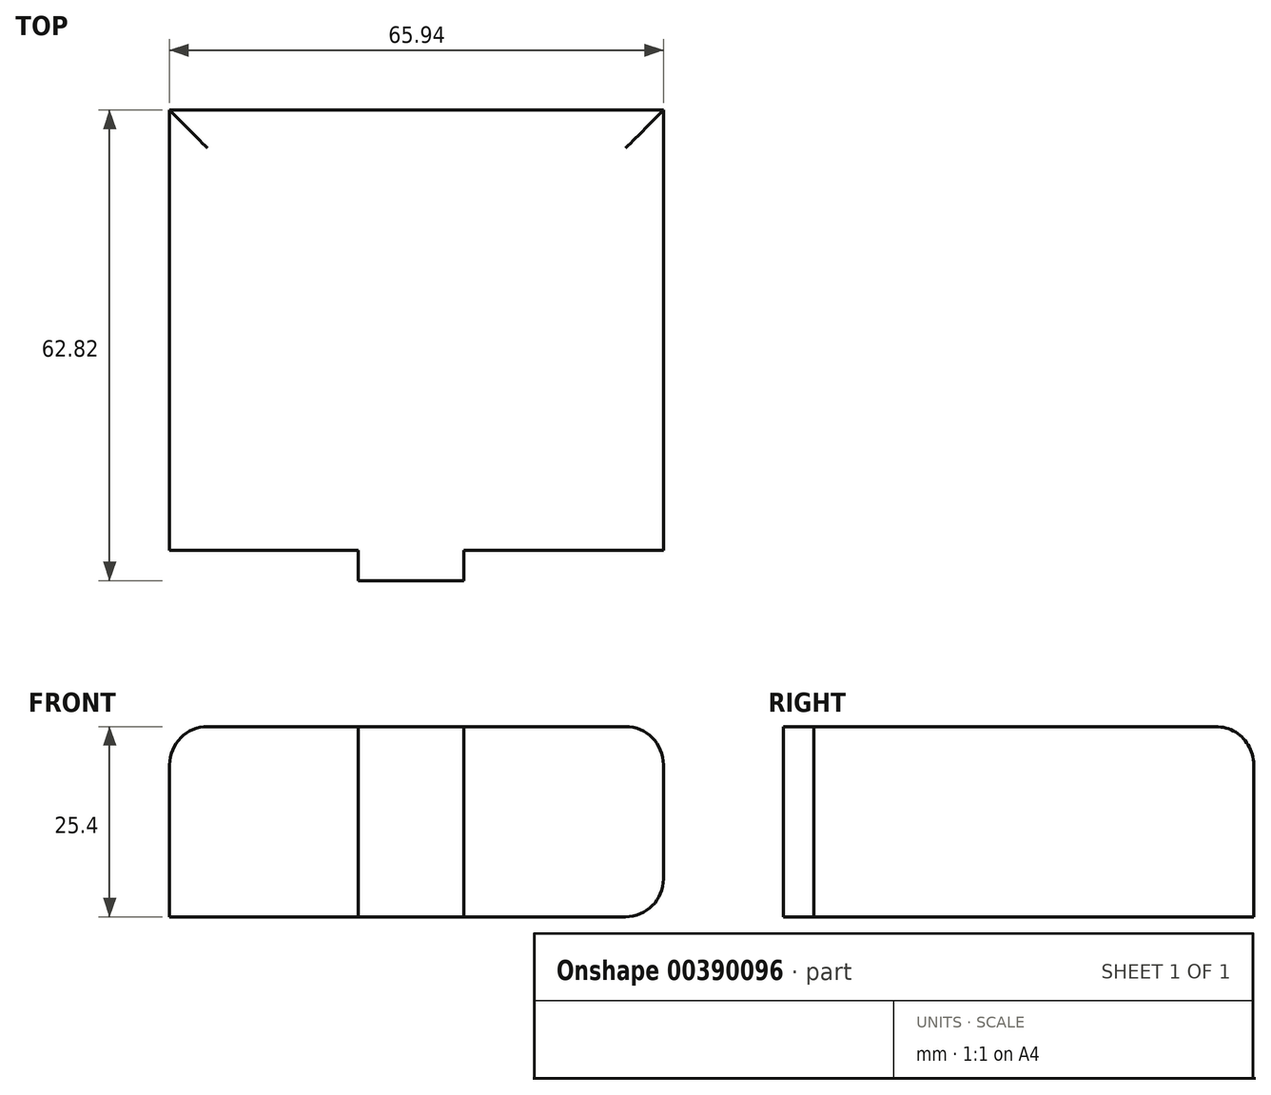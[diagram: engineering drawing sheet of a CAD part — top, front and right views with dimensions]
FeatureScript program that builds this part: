
annotation { "Feature Type Name" : "Feature", "Feature Type Description" : "" }
export const myFeature = defineFeature(function(context is Context, id is Id, definition is map)
    precondition{}
    {
        {
            var Q0;
            Q0=qCreatedBy(makeId("Top.planeOp"),FACE);
            var sketch = newSketch(context, id + "F0", { "sketchPlane" : qUnion([Q0])});
            skLineSegment(sketch, "E0.bottom", {"start": v(-14.1, 65.47) * mm, "end": v(0, 65.47) * mm});
            skLineSegment(sketch, "E0.top", {"start": v(-14.1, 48) * mm, "end": v(0, 48) * mm});
            skLineSegment(sketch, "E0.left", {"start": v(-14.1, 65.47) * mm, "end": v(-14.1, 48) * mm});
            skLineSegment(sketch, "E0.right", {"start": v(0, 65.47) * mm, "end": v(0, 48) * mm});
            skLineSegment(sketch, "E1.bottom", {"start": v(26.66, 52.08) * mm, "end": v(-39.28, 52.08) * mm});
            skLineSegment(sketch, "E1.top", {"start": v(26.66, 110.83) * mm, "end": v(-39.28, 110.83) * mm});
            skLineSegment(sketch, "E1.left", {"start": v(26.66, 52.08) * mm, "end": v(26.66, 110.83) * mm});
            skLineSegment(sketch, "E1.right", {"start": v(-39.28, 52.08) * mm, "end": v(-39.28, 110.83) * mm});
            skSolve(sketch);
        }
        {
            var Q0;
            Q0 = qSketchRegion(id + "F0", true);
            extrude(context, id + "F1", {"entities" : qUnion([Q0]), "depth" : 25.4 * mm});
        }
        {
            var Q0;
            Q0=makeQuery(id+"F1.opExtrude","CAP_EDGE",EDGE,{"disambiguationData":[OSD([sQuery(id+"F0.wireOp",EDGE,"E1.left")])],"isStart":false});
            var Q1;
            Q1=makeQuery(id+"F1.opExtrude","CAP_EDGE",EDGE,{"disambiguationData":[OSD([sQuery(id+"F0.wireOp",EDGE,"E1.left")])],"isStart":true});
            var Q2;
            Q2=makeQuery(id+"F1.opExtrude","CAP_EDGE",EDGE,{"disambiguationData":[OSD([sQuery(id+"F0.wireOp",EDGE,"E1.right")])],"isStart":false});
            var Q3;
            Q3=makeQuery(id+"F1.opExtrude","CAP_EDGE",EDGE,{"disambiguationData":[OSD([sQuery(id+"F0.wireOp",EDGE,"E1.top")])],"isStart":false});
            fillet(context, id + "F2", {"entities" : qUnion([Q0, Q1, Q2, Q3]), "radius" : 5.08 * mm, "tangentPropagation" : true, "allowEdgeOverflow" : false});
        }
    });
